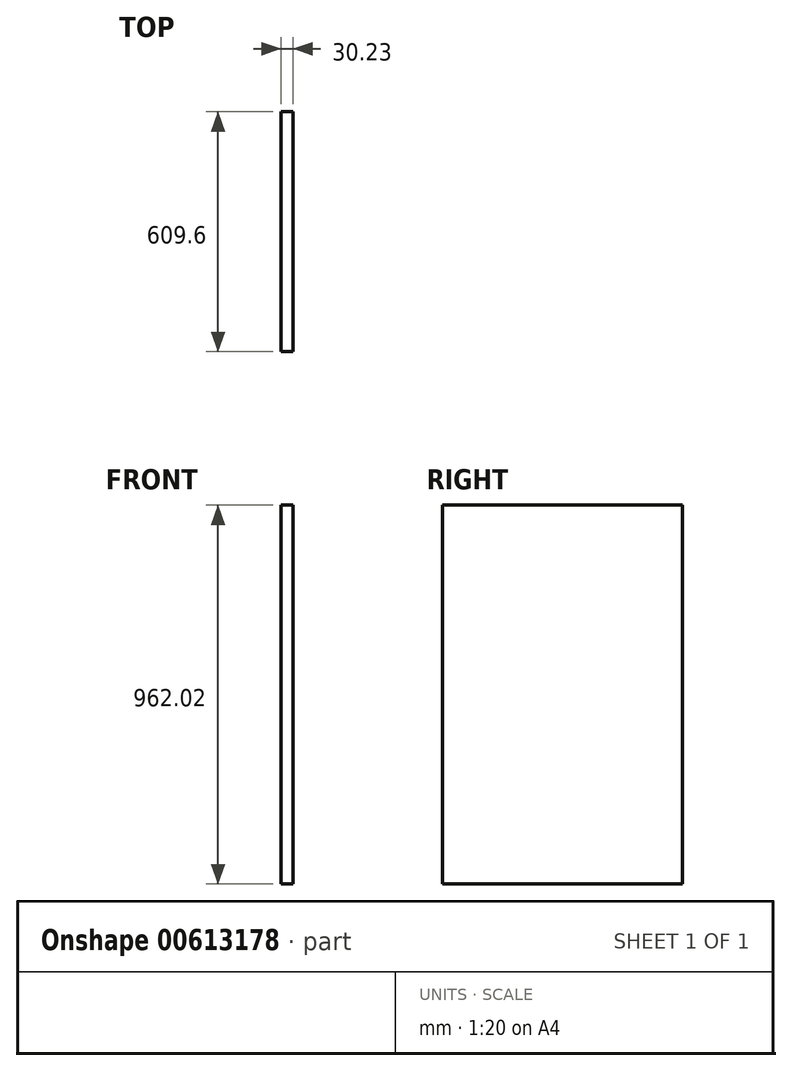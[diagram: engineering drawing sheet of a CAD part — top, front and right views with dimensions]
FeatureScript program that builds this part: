
annotation { "Feature Type Name" : "Feature", "Feature Type Description" : "" }
export const myFeature = defineFeature(function(context is Context, id is Id, definition is map)
    precondition{}
    {
        {
            var Q0;
            Q0=qCreatedBy(makeId("Right.planeOp"),FACE);
            var sketch = newSketch(context, id + "F0", { "sketchPlane" : qUnion([Q0])});
            skLineSegment(sketch, "E0.bottom", {"start": v(304.8, 481.01) * mm, "end": v(-304.8, 481.01) * mm});
            skLineSegment(sketch, "E0.top", {"start": v(304.8, -481.01) * mm, "end": v(-304.8, -481.01) * mm});
            skLineSegment(sketch, "E0.left", {"start": v(304.8, 481.01) * mm, "end": v(304.8, -481.01) * mm});
            skLineSegment(sketch, "E0.right", {"start": v(-304.8, 481.01) * mm, "end": v(-304.8, -481.01) * mm});
            skPoint(sketch, "E0.middle", {"position": v(0, 0) * mm});
            skSolve(sketch);
        }
        {
            var Q0;
            Q0=makeQuery(id+"F0.imprint","IMPRINT",FACE,{"disambiguationData":[TD([[makeQuery(id+"F0.imprint","IMPRINT",EDGE,{"derivedFrom":sQuery(id+"F0.wireOp",EDGE,"E0.bottom")}),1.0]])]});
            extrude(context, id + "F1", {"entities" : qUnion([Q0]), "depth" : 30.23 * mm, "offsetDistance" : 25.4 * mm});
        }
    });
